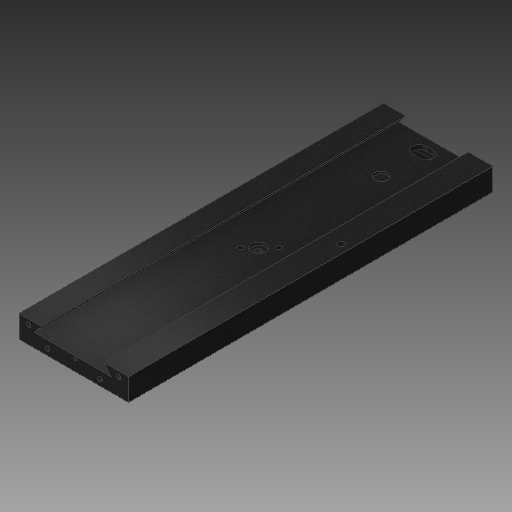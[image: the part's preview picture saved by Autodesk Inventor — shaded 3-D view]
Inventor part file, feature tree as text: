
AUTODESK INVENTOR PART (.ipt)
format: ipt  version: 2018 (Build 220112000, 112)  size: 270,336 bytes
history: native  units: mm
features: extrude x8, sketch x7, reference x5, hole x3, thread x1
ambient origin geometry x8: Origin, YZ Plane, XZ Plane, XY Plane, X Axis, Y Axis, Z Axis, Center Point
bodies: Solid1 (feature_tree)
feature tree (24):
  extrude  "Extrusion1"  Depth=29.6mm
  sketch  "Sketch2"  dims[d2=29.9mm d4=22.68928mm]
  sketch  "Sketch3"  dims[d5=33.0mm d6=8.726646mm]
  extrude  "Extrusion2"  Depth=22.68928mm
  extrude  "Extrusion3"  Depth=8.726646mm
  extrude  "Extrusion4"  Depth=486.0mm
  sketch  "Sketch4"  dims[d7=486.0mm d8=0.0mm d9=22.0mm]
  extrude  "Extrusion5"  Depth=14.5mm
  extrude  "Extrusion7"  Depth=62.1mm
  extrude  "Extrusion8"  Depth=20.0mm
  sketch  "Sketch5"  dims[d10=124.2mm d11=14.5mm]
  sketch  "Sketch6"  dims[d12=62.1mm d13=104.0mm]
  hole  "Hole1"  [1 undecoded]
  hole  "Hole2"  [1 undecoded]
  hole  "Hole3"  [1 undecoded]
  thread  "Thread1"  [1 undecoded]
  extrude  "Extrusion9"  Depth=3.7mm TaperAngle=0.0deg
  sketch  "Sketch1"  dims[d0=146.0mm d1=29.6mm]
  sketch  "Sketch12"  dims[d14=19.02mm d15=8.2mm d17=13.0mm d18=0.0mm d19=7.5mm d20=0.0mm d21=7.5mm d22=0.0mm d23=19.0mm d24=3.7mm d25=0.0mm d26=9.4mm d29=0.0mm d30=18.7mm d31=18.7mm d36=6.0mm d37=0.0mm d38=17.0mm d39=46.5mm d40=3.0mm d41=0.0mm d42=10.0mm d43=225.0mm d44=60.0mm d45=11.0mm d46=60.5mm d47=250.5mm d48=11.0mm d49=190.5mm d50=11.5mm d51=8.5mm d52=6.0mm d53=11.0mm d54=8.5mm d55=90.0deg d56=8.0mm d57=20.594885mm d58=7.0mm d59=6.0mm d60=10.0mm d61=7.5mm d62=90.0deg d63=8.0mm d64=20.594885mm d65=7.5mm d66=6.0mm d67=11.0mm d68=7.0mm d69=90.0deg d70=8.0mm d71=20.594885mm d75=10.0mm d76=0.0mm d77=20.0mm d78=0.0mm]
  reference  "Reference1"
  reference  "Reference2"
  reference  "Reference3"
  reference  "Reference4"
  reference  "Reference5"
note: 4 required parameter values undecoded (feature->parameter linkage not recoverable at this tier; creation-order binding heuristic only, values carry confidence <= 0.55)
